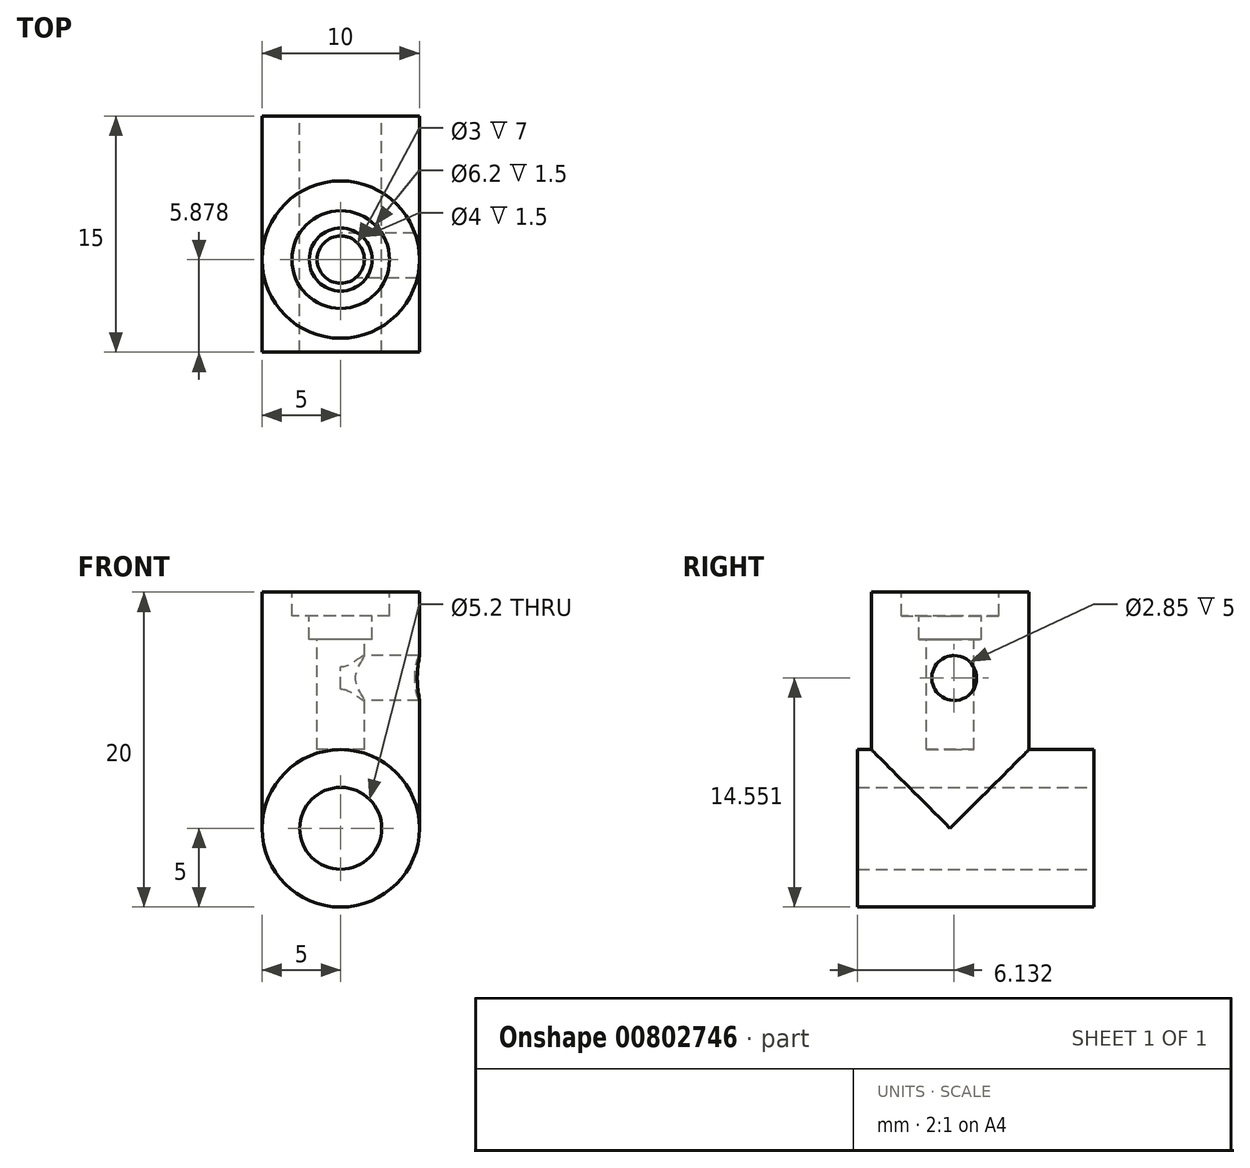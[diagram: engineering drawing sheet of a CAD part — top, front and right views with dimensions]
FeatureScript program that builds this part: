
annotation { "Feature Type Name" : "Feature", "Feature Type Description" : "" }
export const myFeature = defineFeature(function(context is Context, id is Id, definition is map)
    precondition{}
    {
        {
            var Q0;
            Q0=qCreatedBy(makeId("Front.planeOp"),FACE);
            var sketch = newSketch(context, id + "F0", { "sketchPlane" : qUnion([Q0])});
            skCircle(sketch, "E0", {"center": v(0, 0) * mm, "radius": 5 * mm});
            skSolve(sketch);
        }
        {
            var Q0;
            Q0 = qSketchRegion(id + "F0", true);
            extrude(context, id + "F1", {"entities" : qUnion([Q0]), "depth" : 15 * mm, "offsetDistance" : 25 * mm});
        }
        {
            var Q0;
            Q0=qCreatedBy(makeId("Top.planeOp"),FACE);
            var sketch = newSketch(context, id + "F2", { "sketchPlane" : qUnion([Q0])});
            skCircle(sketch, "E1", {"center": v(0, -9.12) * mm, "radius": 5 * mm});
            skSolve(sketch);
        }
        {
            var Q0;
            Q0=qCreatedBy(makeId("Front.planeOp"),FACE);
            var sketch = newSketch(context, id + "F3", { "sketchPlane" : qUnion([Q0])});
            skCircle(sketch, "E2", {"center": v(0, 0) * mm, "radius": 2.6 * mm});
            skSolve(sketch);
        }
        {
            var Q0;
            Q0 = qSketchRegion(id + "F2", true);
            extrude(context, id + "F4", {"entities" : qUnion([Q0]), "operationType" : NewBodyOperationType.ADD, "depth" : 15 * mm, "offsetDistance" : 25 * mm});
        }
        {
            var Q0;
            Q0=makeQuery(id+"F3.imprint","IMPRINT",FACE,{"disambiguationData":[TD([[makeQuery(id+"F3.imprint","IMPRINT",EDGE,{"derivedFrom":sQuery(id+"F3.wireOp",EDGE,"E2")}),1.0]])]});
            extrude(context, id + "F5", {"entities" : qUnion([Q0]), "operationType" : NewBodyOperationType.REMOVE, "depth" : 25 * mm, "offsetDistance" : 25 * mm});
        }
        {
            var Q0;
            Q0=makeQuery(id+"F4.opExtrude","CAP_FACE",FACE,{"disambiguationData":[OSD([sQuery(id+"F2.wireOp",EDGE,"E1")])],"isStart":false});
            var sketch = newSketch(context, id + "F6", { "sketchPlane" : qUnion([Q0])});
            skCircle(sketch, "E3", {"center": v(0, -9.12) * mm, "radius": 1.5 * mm});
            skSolve(sketch);
        }
        {
            var Q0;
            Q0 = qSketchRegion(id + "F6", true);
            extrude(context, id + "F7", {"entities" : qUnion([Q0]), "operationType" : NewBodyOperationType.REMOVE, "oppositeDirection" : true, "depth" : 10 * mm, "offsetDistance" : 25 * mm});
        }
        {
            var Q0;
            Q0=makeQuery(id+"F4.opExtrude","CAP_FACE",FACE,{"disambiguationData":[OSD([sQuery(id+"F2.wireOp",EDGE,"E1")])],"isStart":false});
            var sketch = newSketch(context, id + "F8", { "sketchPlane" : qUnion([Q0])});
            skCircle(sketch, "E4", {"center": v(0, -9.12) * mm, "radius": 3.1 * mm});
            skSolve(sketch);
        }
        {
            var Q0;
            Q0 = qSketchRegion(id + "F8", true);
            extrude(context, id + "F9", {"entities" : qUnion([Q0]), "operationType" : NewBodyOperationType.REMOVE, "oppositeDirection" : true, "depth" : 1.5 * mm, "offsetDistance" : 25 * mm});
        }
        {
            var Q0;
            Q0=qCreatedBy(makeId("Right.planeOp"),FACE);
            var sketch = newSketch(context, id + "F10", { "sketchPlane" : qUnion([Q0])});
            skCircle(sketch, "E5", {"center": v(-8.87, 9.55) * mm, "radius": 1.43 * mm});
            skSolve(sketch);
        }
        {
            var Q0;
            Q0 = qSketchRegion(id + "F10", true);
            extrude(context, id + "F11", {"entities" : qUnion([Q0]), "operationType" : NewBodyOperationType.REMOVE, "depth" : 25 * mm, "offsetDistance" : 25 * mm});
        }
        {
            var Q0;
            Q0=makeQuery(id+"F9.boolean.opBoolean","COPY",FACE,{"derivedFrom":makeQuery(id+"F9.opExtrude","CAP_FACE",FACE,{"disambiguationData":[OSD([sQuery(id+"F8.wireOp",EDGE,"E4")])],"isStart":false})});
            var sketch = newSketch(context, id + "F12", { "sketchPlane" : qUnion([Q0])});
            skCircle(sketch, "E6", {"center": v(0, -9.12) * mm, "radius": 2 * mm});
            skSolve(sketch);
        }
        {
            var Q0;
            Q0 = qSketchRegion(id + "F12", true);
            extrude(context, id + "F13", {"entities" : qUnion([Q0]), "operationType" : NewBodyOperationType.REMOVE, "oppositeDirection" : true, "depth" : 1.5 * mm, "offsetDistance" : 25 * mm});
        }
    });
